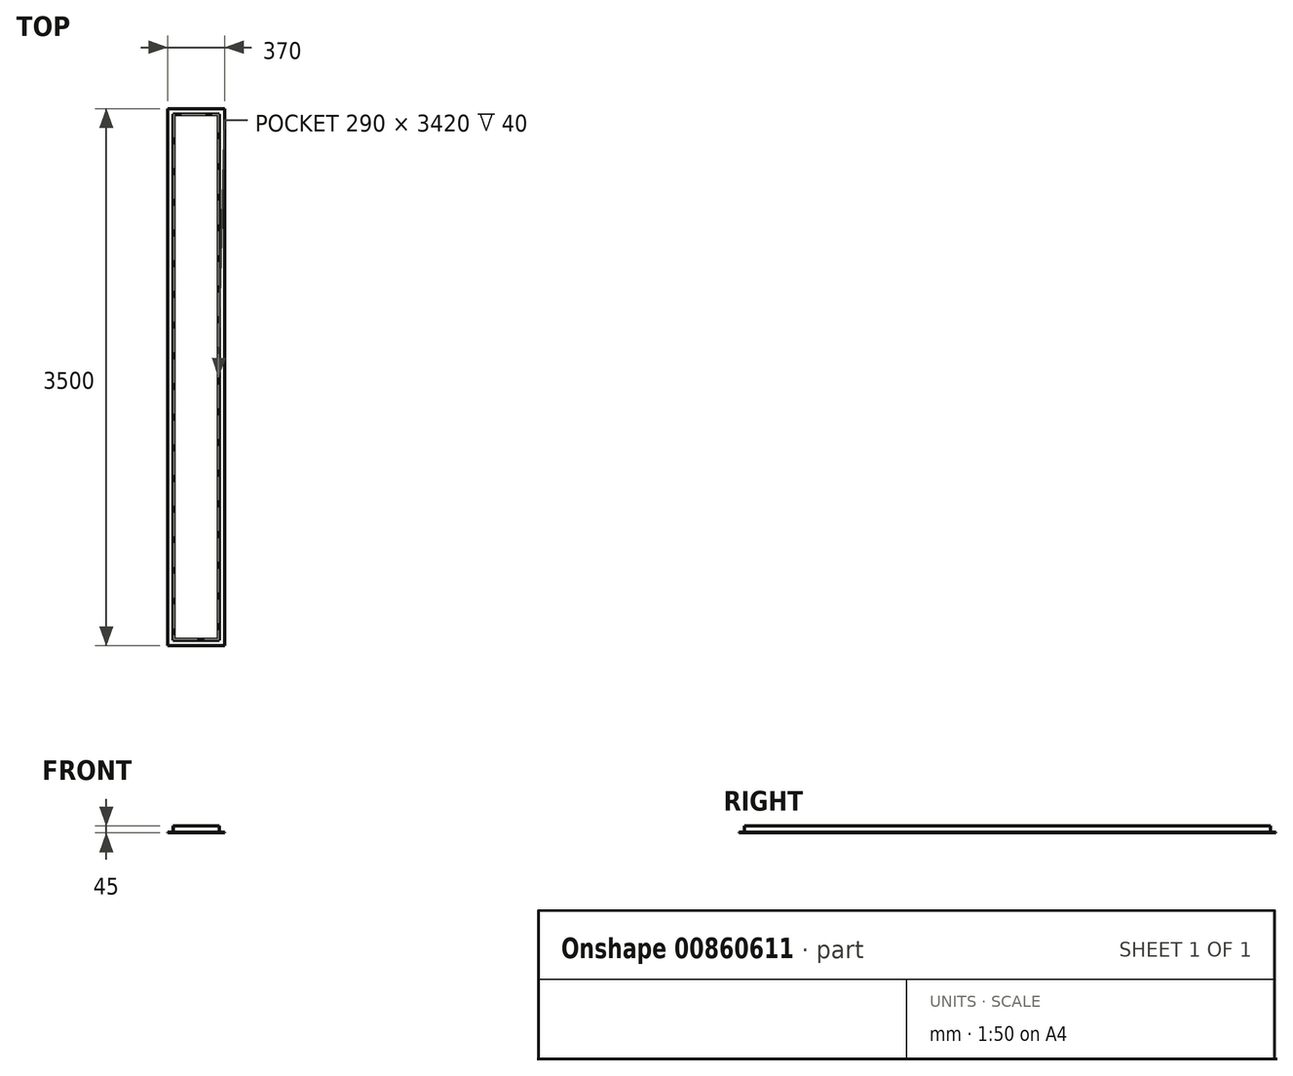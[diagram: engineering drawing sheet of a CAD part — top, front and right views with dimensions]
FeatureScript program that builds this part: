
annotation { "Feature Type Name" : "Feature", "Feature Type Description" : "" }
export const myFeature = defineFeature(function(context is Context, id is Id, definition is map)
    precondition{}
    {
        {
            var Q0;
            Q0=qCreatedBy(makeId("Top.planeOp"),FACE);
            var sketch = newSketch(context, id + "F0", { "sketchPlane" : qUnion([Q0])});
            skLineSegment(sketch, "E0.bottom", {"start": v(-185, 1750) * mm, "end": v(185, 1750) * mm});
            skLineSegment(sketch, "E0.top", {"start": v(-185, -1750) * mm, "end": v(185, -1750) * mm});
            skLineSegment(sketch, "E0.left", {"start": v(-185, 1750) * mm, "end": v(-185, -1750) * mm});
            skLineSegment(sketch, "E0.right", {"start": v(185, 1750) * mm, "end": v(185, -1750) * mm});
            skLineSegment(sketch, "E1", {"start": v(0, 426.2) * mm, "end": v(0, -404.43) * mm, "construction": true});
            skLineSegment(sketch, "E2", {"start": v(-392.17, 0) * mm, "end": v(335.4, 0) * mm, "construction": true});
            skSolve(sketch);
        }
        {
            var Q0;
            Q0 = qSketchRegion(id + "F0", true);
            extrude(context, id + "F1", {"entities" : qUnion([Q0]), "depth" : 5 * mm, "offsetDistance" : 25.4 * mm});
        }
        {
            var Q0;
            Q0=makeQuery(id+"F1.opExtrude","CAP_FACE",FACE,{"disambiguationData":[OSD([sQuery(id+"F0.wireOp",EDGE,"E0.bottom"),sQuery(id+"F0.wireOp",EDGE,"E0.top"),sQuery(id+"F0.wireOp",EDGE,"E0.left"),sQuery(id+"F0.wireOp",EDGE,"E0.right")])],"isStart":false});
            var sketch = newSketch(context, id + "F2", { "sketchPlane" : qUnion([Q0])});
            skLineSegment(sketch, "E3.bottom", {"start": v(-150, 1715) * mm, "end": v(150, 1715) * mm});
            skLineSegment(sketch, "E3.top", {"start": v(-150, -1715) * mm, "end": v(150, -1715) * mm});
            skLineSegment(sketch, "E3.left", {"start": v(-150, 1715) * mm, "end": v(-150, -1715) * mm});
            skLineSegment(sketch, "E3.right", {"start": v(150, 1715) * mm, "end": v(150, -1715) * mm});
            skLineSegment(sketch, "E4.0", {"start": v(-145, 1710) * mm, "end": v(-145, -1710) * mm});
            skLineSegment(sketch, "E4.1", {"start": v(-145, 1710) * mm, "end": v(145, 1710) * mm});
            skLineSegment(sketch, "E4.2", {"start": v(145, 1710) * mm, "end": v(145, -1710) * mm});
            skLineSegment(sketch, "E4.3", {"start": v(-145, -1710) * mm, "end": v(145, -1710) * mm});
            skSolve(sketch);
        }
        {
            var Q0;
            Q0 = qSketchRegion(id + "F2", true);
            extrude(context, id + "F3", {"entities" : qUnion([Q0]), "operationType" : NewBodyOperationType.ADD, "depth" : 40 * mm, "offsetDistance" : 25.4 * mm});
        }
    });
